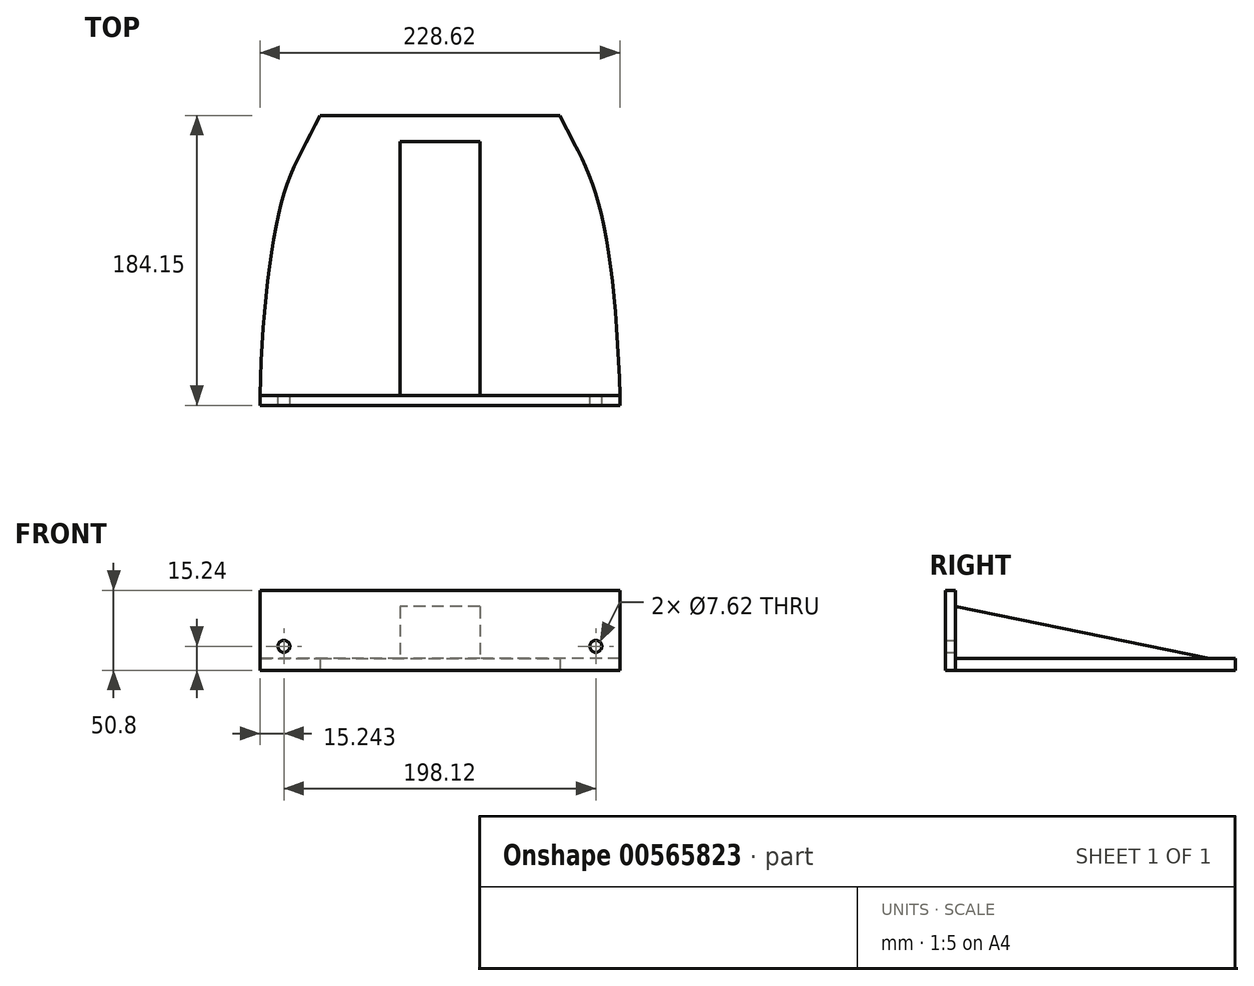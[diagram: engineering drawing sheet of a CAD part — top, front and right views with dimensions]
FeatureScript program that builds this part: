
annotation { "Feature Type Name" : "Feature", "Feature Type Description" : "" }
export const myFeature = defineFeature(function(context is Context, id is Id, definition is map)
    precondition{}
    {
        {
            var Q0;
            Q0=qCreatedBy(makeId("Top.planeOp"),FACE);
            var sketch = newSketch(context, id + "F0", { "sketchPlane" : qUnion([Q0])});
            skLineSegment(sketch, "E0", {"start": v(0, 0) * mm, "end": v(-114.3, 0) * mm});
            skLineSegment(sketch, "E1.MirrorCS", {"start": v(0, 0) * mm, "end": v(114.3, 0) * mm});
            skLineSegment(sketch, "E2", {"start": v(0, 177.8) * mm, "end": v(-76.2, 177.8) * mm});
            skLineSegment(sketch, "E3.MirrorCS", {"start": v(0, 177.8) * mm, "end": v(76.2, 177.8) * mm});
            skFitSpline(sketch, "E4", {"points": [v(-114.3, 0) * mm, v(-99.1, 127.79) * mm, v(-76.2, 177.8) * mm], "startDerivative": vector(6.92, 252.98) * mm, "endDerivative": vector(72.41, 148.42) * mm});
            skFitSpline(sketch, "E5.MirrorCS", {"points": [v(114.3, 0) * mm, v(99.1, 127.79) * mm, v(76.2, 177.8) * mm], "startDerivative": vector(-6.92, 252.98) * mm, "endDerivative": vector(-72.41, 148.42) * mm});
            skSolve(sketch);
        }
        {
            var Q0;
            Q0=qCreatedBy(makeId("Front.planeOp"),FACE);
            var sketch = newSketch(context, id + "F1", { "sketchPlane" : qUnion([Q0])});
            skLineSegment(sketch, "E6.bottom", {"start": v(-114.32, 0) * mm, "end": v(114.28, 0) * mm});
            skLineSegment(sketch, "E6.top", {"start": v(-114.32, 50.8) * mm, "end": v(114.28, 50.8) * mm});
            skLineSegment(sketch, "E6.left", {"start": v(-114.32, 0) * mm, "end": v(-114.32, 50.8) * mm});
            skLineSegment(sketch, "E6.right", {"start": v(114.28, 0) * mm, "end": v(114.28, 50.8) * mm});
            skCircle(sketch, "E7", {"center": v(99.04, 15.24) * mm, "radius": 3.8 * mm});
            skCircle(sketch, "E8", {"center": v(-99.08, 15.24) * mm, "radius": 3.81 * mm});
            skSolve(sketch);
        }
        {
            var Q0;
            Q0 = qSketchRegion(id + "F1", true);
            extrude(context, id + "F2", {"entities" : qUnion([Q0]), "depth" : 6.35 * mm, "offsetDistance" : 25.4 * mm});
        }
        {
            var Q0;
            Q0=makeQuery(id+"F0.imprint","IMPRINT",FACE,{"disambiguationData":[TD([[makeQuery(id+"F0.imprint","IMPRINT",EDGE,{"derivedFrom":sQuery(id+"F0.wireOp",EDGE,"E0")}),-1.0]])]});
            extrude(context, id + "F3", {"entities" : qUnion([Q0]), "operationType" : NewBodyOperationType.ADD, "depth" : 7.62 * mm, "offsetDistance" : 25.4 * mm});
        }
        {
            var Q0;
            Q0=qCreatedBy(makeId("Right.planeOp"),FACE);
            var sketch = newSketch(context, id + "F4", { "sketchPlane" : qUnion([Q0])});
            skLineSegment(sketch, "E9", {"start": v(0, 40.46) * mm, "end": v(0, 7.62) * mm});
            skLineSegment(sketch, "E10", {"start": v(0, 7.62) * mm, "end": v(161.22, 7.62) * mm});
            skLineSegment(sketch, "E11", {"start": v(161.22, 7.62) * mm, "end": v(0, 40.46) * mm});
            skSolve(sketch);
        }
        {
            var Q0;
            Q0=makeQuery(id+"F4.imprint","IMPRINT",FACE,{"disambiguationData":[TD([[makeQuery(id+"F4.imprint","IMPRINT",EDGE,{"derivedFrom":sQuery(id+"F4.wireOp",EDGE,"E9")}),1.0]])]});
            extrude(context, id + "F5", {"entities" : qUnion([Q0]), "operationType" : NewBodyOperationType.ADD, "depth" : 25.4 * mm, "offsetDistance" : 25.4 * mm, "hasSecondDirection" : true, "secondDirectionOppositeDirection" : true, "secondDirectionDepth" : 25.4 * mm});
        }
    });
